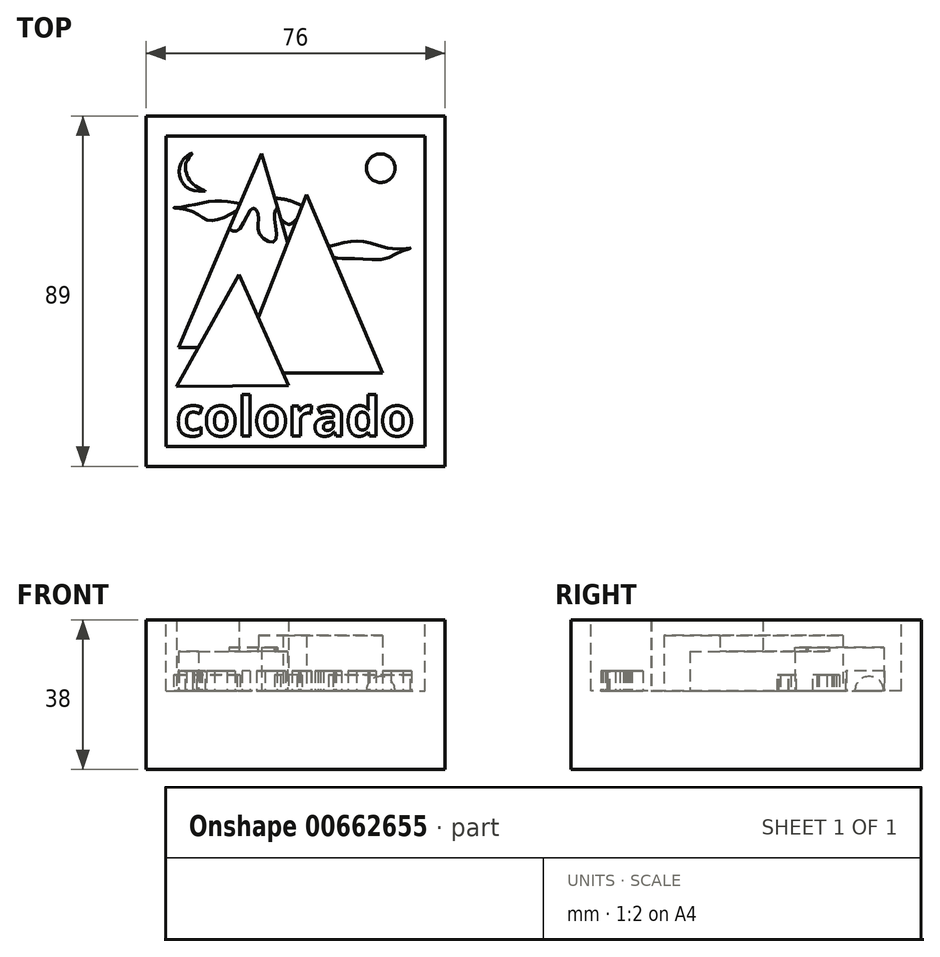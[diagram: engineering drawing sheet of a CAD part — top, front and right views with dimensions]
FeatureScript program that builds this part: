
annotation { "Feature Type Name" : "Feature", "Feature Type Description" : "" }
export const myFeature = defineFeature(function(context is Context, id is Id, definition is map)
    precondition{}
    {
        {
            var Q0;
            Q0=qCreatedBy(makeId("Top.planeOp"),FACE);
            var sketch = newSketch(context, id + "F0", { "sketchPlane" : qUnion([Q0])});
            skLineSegment(sketch, "E0.bottom", {"start": v(-32.78, 51.1) * mm, "end": v(43.22, 51.1) * mm});
            skLineSegment(sketch, "E0.top", {"start": v(-32.78, -37.9) * mm, "end": v(43.22, -37.9) * mm});
            skLineSegment(sketch, "E0.left", {"start": v(-32.78, 51.1) * mm, "end": v(-32.78, -37.9) * mm});
            skLineSegment(sketch, "E0.right", {"start": v(43.22, 51.1) * mm, "end": v(43.22, -37.9) * mm});
            skSolve(sketch);
        }
        {
            var Q0;
            Q0=makeQuery(id+"F0.imprint","IMPRINT",FACE,{"disambiguationData":[TD([[makeQuery(id+"F0.imprint","IMPRINT",EDGE,{"derivedFrom":sQuery(id+"F0.wireOp",EDGE,"E0.bottom")}),-1.0]])]});
            extrude(context, id + "F1", {"entities" : qUnion([Q0]), "depth" : 38 * mm, "offsetDistance" : 25.4 * mm});
        }
        {
            var Q0;
            {var subQ0=sQuery(id+"F0.wireOp",EDGE,"E0.top");var subQ1=sQuery(id+"F0.wireOp",EDGE,"E0.right");var subQ2=sQuery(id+"F0.wireOp",EDGE,"E0.bottom");var subQ3=sQuery(id+"F0.wireOp",EDGE,"E0.left");Q0=makeQuery(id+"F5.boolean.opBoolean","SPLIT",FACE,{"disambiguationData":[TD([makeQuery(id+"F1.opExtrude","SWEPT_FACE",FACE,{"disambiguationData":[OSD([subQ2])]})])],"derivedFrom":makeQuery(id+"F1.opExtrude","CAP_FACE",FACE,{"disambiguationData":[OSD([subQ2,subQ0,subQ3,subQ1])],"isStart":false})});}
            var sketch = newSketch(context, id + "F2", { "sketchPlane" : qUnion([Q0])});
            skLineSegment(sketch, "E1.bottom", {"start": v(-27.7, 46.03) * mm, "end": v(38.14, 46.03) * mm});
            skLineSegment(sketch, "E1.top", {"start": v(-27.7, -32.81) * mm, "end": v(38.14, -32.81) * mm});
            skLineSegment(sketch, "E1.left", {"start": v(-27.7, 46.03) * mm, "end": v(-27.7, -32.81) * mm});
            skLineSegment(sketch, "E1.right", {"start": v(38.14, 46.03) * mm, "end": v(38.14, -32.81) * mm});
            skSolve(sketch);
        }
        {
            var Q0;
            Q0 = qSketchRegion(id + "F2", true);
            extrude(context, id + "F3", {"entities" : qUnion([Q0]), "operationType" : NewBodyOperationType.REMOVE, "oppositeDirection" : true, "depth" : 18 * mm, "offsetDistance" : 25.4 * mm});
        }
        {
            var Q0;
            Q0=makeQuery(id+"F3.boolean.opBoolean","COPY",FACE,{"derivedFrom":makeQuery(id+"F3.opExtrude","CAP_FACE",FACE,{"disambiguationData":[OSD([sQuery(id+"F2.wireOp",EDGE,"E1.bottom"),sQuery(id+"F2.wireOp",EDGE,"E1.top"),sQuery(id+"F2.wireOp",EDGE,"E1.left"),sQuery(id+"F2.wireOp",EDGE,"E1.right")])],"isStart":false})});
            var sketch = newSketch(context, id + "F4", { "sketchPlane" : qUnion([Q0])});
            skText(sketch, "E2", { "text": "colorado", "fontName": "OpenSans-Bold.ttf"});
            const initialGuessF4  = {"E2": [-0.02516, -0.03014, 1, 0, 0.00997]};
            skSetInitialGuess(sketch, initialGuessF4);
            skSolve(sketch);
        }
        {
            var Q0;
            Q0 = qSketchRegion(id + "F4", true);
            extrude(context, id + "F5", {"entities" : qUnion([Q0]), "operationType" : NewBodyOperationType.ADD, "oppositeDirection" : true, "depth" : 0 * mm, "offsetDistance" : 25.4 * mm, "hasSecondDirection" : true, "secondDirectionOppositeDirection" : false, "secondDirectionDepth" : 5 * mm});
        }
        {
            var Q0;
            {var subQ0=sQuery(id+"F2.wireOp",EDGE,"E1.left");var subQ1=sQuery(id+"F2.wireOp",EDGE,"E1.top");var subQ2=sQuery(id+"F2.wireOp",EDGE,"E1.bottom");var subQ3=sQuery(id+"F2.wireOp",EDGE,"E1.right");Q0=makeQuery(id+"F5.boolean.opBoolean","SPLIT",FACE,{"disambiguationData":[TD([makeQuery(id+"F3.boolean.opBoolean","COPY",FACE,{"derivedFrom":makeQuery(id+"F3.opExtrude","SWEPT_FACE",FACE,{"disambiguationData":[OSD([subQ2])]})})])],"derivedFrom":makeQuery(id+"F3.boolean.opBoolean","COPY",FACE,{"derivedFrom":makeQuery(id+"F3.opExtrude","CAP_FACE",FACE,{"disambiguationData":[OSD([subQ2,subQ1,subQ0,subQ3])],"isStart":false})})});}
            var sketch = newSketch(context, id + "F6", { "sketchPlane" : qUnion([Q0])});
            skLineSegment(sketch, "E3", {"start": v(-24.96, -17.63) * mm, "end": v(-9.04, 10.85) * mm});
            skLineSegment(sketch, "E4", {"start": v(-9.04, 10.85) * mm, "end": v(3.51, -17.39) * mm});
            skLineSegment(sketch, "E5", {"start": v(3.51, -17.39) * mm, "end": v(-24.96, -17.63) * mm});
            skSolve(sketch);
        }
        {
            var Q0;
            Q0=makeQuery(id+"F6.imprint","IMPRINT",FACE,{"disambiguationData":[TD([[makeQuery(id+"F6.imprint","IMPRINT",EDGE,{"derivedFrom":sQuery(id+"F6.wireOp",EDGE,"E3")}),-1.0]])]});
            extrude(context, id + "F7", {"entities" : qUnion([Q0]), "operationType" : NewBodyOperationType.ADD, "depth" : 18 * mm, "offsetDistance" : 25.4 * mm});
        }
        {
            var Q0;
            {var subQ0=sQuery(id+"F2.wireOp",EDGE,"E1.left");var subQ1=sQuery(id+"F2.wireOp",EDGE,"E1.top");var subQ2=sQuery(id+"F2.wireOp",EDGE,"E1.bottom");var subQ3=sQuery(id+"F2.wireOp",EDGE,"E1.right");Q0=makeQuery(id+"F5.boolean.opBoolean","SPLIT",FACE,{"disambiguationData":[TD([makeQuery(id+"F3.boolean.opBoolean","COPY",FACE,{"derivedFrom":makeQuery(id+"F3.opExtrude","SWEPT_FACE",FACE,{"disambiguationData":[OSD([subQ2])]})})])],"derivedFrom":makeQuery(id+"F3.boolean.opBoolean","COPY",FACE,{"derivedFrom":makeQuery(id+"F3.opExtrude","CAP_FACE",FACE,{"disambiguationData":[OSD([subQ2,subQ1,subQ0,subQ3])],"isStart":false})})});}
            var sketch = newSketch(context, id + "F8", { "sketchPlane" : qUnion([Q0])});
            skLineSegment(sketch, "E6", {"start": v(2.1, -14.22) * mm, "end": v(27.39, -14.22) * mm});
            skLineSegment(sketch, "E7", {"start": v(27.39, -14.22) * mm, "end": v(8.01, 31.18) * mm});
            skLineSegment(sketch, "E8", {"start": v(8.01, 31.18) * mm, "end": v(-4.22, 0) * mm});
            skLineSegment(sketch, "E9", {"start": v(-4.22, 0) * mm, "end": v(2.1, -14.22) * mm});
            skSolve(sketch);
        }
        {
            var Q0;
            Q0 = qSketchRegion(id + "F8", true);
            extrude(context, id + "F9", {"entities" : qUnion([Q0]), "operationType" : NewBodyOperationType.ADD, "depth" : 14 * mm, "offsetDistance" : 25.4 * mm});
        }
        {
            var Q0;
            {var subQ0=sQuery(id+"F2.wireOp",EDGE,"E1.left");var subQ1=sQuery(id+"F2.wireOp",EDGE,"E1.top");var subQ2=sQuery(id+"F2.wireOp",EDGE,"E1.bottom");var subQ3=sQuery(id+"F2.wireOp",EDGE,"E1.right");Q0=makeQuery(id+"F5.boolean.opBoolean","SPLIT",FACE,{"disambiguationData":[TD([makeQuery(id+"F3.boolean.opBoolean","COPY",FACE,{"derivedFrom":makeQuery(id+"F3.opExtrude","SWEPT_FACE",FACE,{"disambiguationData":[OSD([subQ2])]})})])],"derivedFrom":makeQuery(id+"F3.boolean.opBoolean","COPY",FACE,{"derivedFrom":makeQuery(id+"F3.opExtrude","CAP_FACE",FACE,{"disambiguationData":[OSD([subQ2,subQ1,subQ0,subQ3])],"isStart":false})})});}
            var sketch = newSketch(context, id + "F10", { "sketchPlane" : qUnion([Q0])});
            skLineSegment(sketch, "E10", {"start": v(-19.4, -7.68) * mm, "end": v(-24.53, -7.68) * mm});
            skLineSegment(sketch, "E11", {"start": v(-24.53, -7.68) * mm, "end": v(-3.41, 41.62) * mm});
            skLineSegment(sketch, "E12", {"start": v(-3.41, 41.62) * mm, "end": v(3.23, 19) * mm});
            skLineSegment(sketch, "E13", {"start": v(3.23, 19) * mm, "end": v(-4.22, 0) * mm});
            skLineSegment(sketch, "E14", {"start": v(-4.22, 0) * mm, "end": v(-9.04, 10.85) * mm});
            skLineSegment(sketch, "E15", {"start": v(-9.04, 10.85) * mm, "end": v(-19.4, -7.68) * mm});
            skSolve(sketch);
        }
        {
            var Q0;
            Q0=makeQuery(id+"F10.imprint","IMPRINT",FACE,{"disambiguationData":[TD([[makeQuery(id+"F10.imprint","IMPRINT",EDGE,{"derivedFrom":sQuery(id+"F10.wireOp",EDGE,"E10")}),-1.0]])]});
            extrude(context, id + "F11", {"entities" : qUnion([Q0]), "operationType" : NewBodyOperationType.ADD, "depth" : 10 * mm, "offsetDistance" : 25.4 * mm});
        }
        {
            var Q0;
            Q0=makeQuery(id+"F11.opExtrude","CAP_FACE",FACE,{"disambiguationData":[OSD([sQuery(id+"F10.wireOp",EDGE,"E10"),sQuery(id+"F10.wireOp",EDGE,"E11"),sQuery(id+"F10.wireOp",EDGE,"E12"),sQuery(id+"F10.wireOp",EDGE,"E13"),sQuery(id+"F10.wireOp",EDGE,"E14"),sQuery(id+"F10.wireOp",EDGE,"E15")])],"isStart":false});
            var sketch = newSketch(context, id + "F12", { "sketchPlane" : qUnion([Q0])});
            skPoint(sketch, "E16.1.internal.snap0", {"position": v(-0.1, 30.3) * mm});
            skPoint(sketch, "E16.2.internal.snap0", {"position": v(-0.1, 30.3) * mm});
            skFitSpline(sketch, "E16", {"points": [v(0.64, 27.8) * mm, v(-0.1, 25.97) * mm, v(-0.1, 19.26) * mm, v(-3.91, 21.25) * mm, v(-4.16, 25.72) * mm, v(-5.65, 27.7) * mm, v(-9.13, 22.24) * mm, v(-11.66, 22.37) * mm], "startDerivative": vector(-10.56, -12.1) * mm, "endDerivative": vector(-22.67, 10.78) * mm});
            skLineSegment(sketch, "E17", {"start": v(-11.66, 22.37) * mm, "end": v(-3.41, 41.62) * mm});
            skLineSegment(sketch, "E18", {"start": v(-3.41, 41.62) * mm, "end": v(0.64, 27.8) * mm});
            skSolve(sketch);
        }
        {
            var Q0;
            Q0 = qSketchRegion(id + "F12", true);
            extrude(context, id + "F13", {"entities" : qUnion([Q0]), "operationType" : NewBodyOperationType.ADD, "depth" : 1 * mm, "offsetDistance" : 25.4 * mm});
        }
        {
            var Q0;
            {var subQ0=sQuery(id+"F2.wireOp",EDGE,"E1.left");var subQ1=sQuery(id+"F2.wireOp",EDGE,"E1.top");var subQ2=sQuery(id+"F2.wireOp",EDGE,"E1.bottom");var subQ3=sQuery(id+"F2.wireOp",EDGE,"E1.right");Q0=makeQuery(id+"F5.boolean.opBoolean","SPLIT",FACE,{"disambiguationData":[TD([makeQuery(id+"F3.boolean.opBoolean","COPY",FACE,{"derivedFrom":makeQuery(id+"F3.opExtrude","SWEPT_FACE",FACE,{"disambiguationData":[OSD([subQ2])]})})])],"derivedFrom":makeQuery(id+"F3.boolean.opBoolean","COPY",FACE,{"derivedFrom":makeQuery(id+"F3.opExtrude","CAP_FACE",FACE,{"disambiguationData":[OSD([subQ2,subQ1,subQ0,subQ3])],"isStart":false})})});}
            var sketch = newSketch(context, id + "F14", { "sketchPlane" : qUnion([Q0])});
            skArc(sketch, "E19", {"start": v(29.86, 35.8) * mm, "mid": v(28.95, 40.86) * mm, "end": v(23.9, 39.95) * mm});
            skLineSegment(sketch, "E20", {"start": v(23.9, 39.95) * mm, "end": v(29.86, 35.8) * mm});
            skSolve(sketch);
        }
        {
            var Q0;
            Q0=makeQuery(id+"F14.imprint","IMPRINT",FACE,{"disambiguationData":[TD([[makeQuery(id+"F14.imprint","IMPRINT",EDGE,{"derivedFrom":sQuery(id+"F14.wireOp",EDGE,"E19")}),1.0]])]});
            var Q1;
            Q1=sQuery(id+"F14.wireOp",EDGE,"E20");
            revolve(context, id + "F15", {"operationType" : NewBodyOperationType.ADD, "entities" : qUnion([Q0]), "axis" : qUnion([Q1]), "revolveType" : RevolveType.FULL});
        }
        {
            var Q0;
            {var subQ0=sQuery(id+"F2.wireOp",EDGE,"E1.left");var subQ1=sQuery(id+"F2.wireOp",EDGE,"E1.top");var subQ2=sQuery(id+"F2.wireOp",EDGE,"E1.bottom");var subQ3=sQuery(id+"F2.wireOp",EDGE,"E1.right");Q0=makeQuery(id+"F5.boolean.opBoolean","SPLIT",FACE,{"disambiguationData":[TD([makeQuery(id+"F3.boolean.opBoolean","COPY",FACE,{"derivedFrom":makeQuery(id+"F3.opExtrude","SWEPT_FACE",FACE,{"disambiguationData":[OSD([subQ2])]})})])],"derivedFrom":makeQuery(id+"F3.boolean.opBoolean","COPY",FACE,{"derivedFrom":makeQuery(id+"F3.opExtrude","CAP_FACE",FACE,{"disambiguationData":[OSD([subQ2,subQ1,subQ0,subQ3])],"isStart":false})})});}
            var sketch = newSketch(context, id + "F16", { "sketchPlane" : qUnion([Q0])});
            skFitSpline(sketch, "E21", {"points": [v(13.63, 18.02) * mm, v(19.1, 19.26) * mm, v(22.99, 19.18) * mm, v(30.15, 17.39) * mm, v(34.48, 17.52) * mm, v(32.51, 16.9) * mm, v(27.49, 14.76) * mm, v(20.1, 14.98) * mm, v(16.52, 14.9) * mm, v(14.8, 15.28) * mm], "startDerivative": vector(46, 11.91) * mm, "endDerivative": vector(-22.84, 7.22) * mm});
            skLineSegment(sketch, "E22", {"start": v(13.63, 18.02) * mm, "end": v(14.8, 15.28) * mm});
            skPoint(sketch, "E23.2.internal.snap0", {"position": v(5.62, 25.09) * mm});
            skFitSpline(sketch, "E23", {"points": [v(5.62, 25.09) * mm, v(3.58, 23.6) * mm, v(1.44, 25.09) * mm], "startDerivative": vector(-4.07, -4.47) * mm, "endDerivative": vector(-4.29, 4.44) * mm});
            skFitSpline(sketch, "E24", {"points": [v(6.9, 28.35) * mm, v(3.23, 29.77) * mm, v(-0.1, 30.3) * mm], "startDerivative": vector(-7.1, 3.15) * mm, "endDerivative": vector(-6.88, 0.73) * mm});
            skLineSegment(sketch, "E25", {"start": v(-0.1, 30.3) * mm, "end": v(1.44, 25.09) * mm});
            skLineSegment(sketch, "E26", {"start": v(6.9, 28.35) * mm, "end": v(5.62, 25.09) * mm});
            skFitSpline(sketch, "E27", {"points": [v(-8.87, 28.87) * mm, v(-15.5, 29.5) * mm, v(-23.12, 28.1) * mm, v(-25.7, 27.78) * mm, v(-21.2, 26.93) * mm, v(-16.47, 24.57) * mm, v(-9.63, 27.1) * mm], "startDerivative": vector(-35.33, 6.52) * mm, "endDerivative": vector(38.93, 21.85) * mm});
            skLineSegment(sketch, "E28", {"start": v(-8.87, 28.87) * mm, "end": v(-9.63, 27.1) * mm});
            skSolve(sketch);
        }
        {
            var Q0;
            {var subQ65=sQuery(id+"F2.wireOp",EDGE,"E1.bottom");Q0=makeQuery(id+"F16.imprint","IMPRINT",FACE,{"disambiguationData":[TD([[makeQuery(id+"F16.imprint","IMPRINT",EDGE,{"derivedFrom":makeQuery(id+"F3.boolean.opBoolean","COPY",EDGE,{"derivedFrom":makeQuery(id+"F3.opExtrude","CAP_EDGE",EDGE,{"disambiguationData":[OSD([subQ65])],"isStart":false})})}),-1.0]])]});}
            var sketch = newSketch(context, id + "F17", { "sketchPlane" : qUnion([Q0])});
            skArc(sketch, "E29", {"start": v(-20.9, 41.72) * mm, "mid": v(-24.3, 36.8) * mm, "end": v(-20.54, 32.13) * mm});
            skFitSpline(sketch, "E30", {"points": [v(-20.9, 41.72) * mm, v(-22.27, 39.91) * mm, v(-22.7, 38.86) * mm, v(-22.62, 37.11) * mm, v(-22.1, 35.54) * mm, v(-20.9, 33.88) * mm, v(-18.68, 32.48) * mm, v(-17.63, 32.04) * mm, v(-20.54, 32.13) * mm], "startDerivative": vector(-11.42, -14.23) * mm, "endDerivative": vector(-27.87, 1.93) * mm});
            skSolve(sketch);
        }
        {
            var Q0;
            Q0=makeQuery(id+"F17.imprint","IMPRINT",FACE,{"disambiguationData":[TD([[makeQuery(id+"F17.imprint","IMPRINT",EDGE,{"derivedFrom":sQuery(id+"F17.wireOp",EDGE,"E29")}),1.0]])]});
            extrude(context, id + "F18", {"entities" : qUnion([Q0]), "operationType" : NewBodyOperationType.ADD, "depth" : 5 * mm, "offsetDistance" : 25.4 * mm});
        }
        {
            var Q0;
            Q0=makeQuery(id+"F16.imprint","IMPRINT",FACE,{"disambiguationData":[TD([[makeQuery(id+"F16.imprint","IMPRINT",EDGE,{"derivedFrom":sQuery(id+"F16.wireOp",EDGE,"E21")}),-1.0]])]});
            extrude(context, id + "F19", {"entities" : qUnion([Q0]), "operationType" : NewBodyOperationType.ADD, "depth" : 3 * mm, "offsetDistance" : 25.4 * mm});
        }
        {
            var Q0;
            Q0 = qSketchRegion(id + "F16", true);
            extrude(context, id + "F20", {"entities" : qUnion([Q0]), "operationType" : NewBodyOperationType.ADD, "depth" : 4 * mm, "offsetDistance" : 25.4 * mm});
        }
    });
